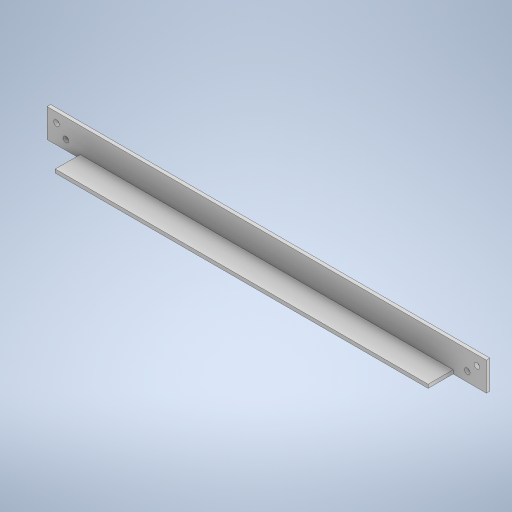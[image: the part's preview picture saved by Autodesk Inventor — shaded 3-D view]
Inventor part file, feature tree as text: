
AUTODESK INVENTOR PART (.ipt)
format: ipt  version: 2023 (Build 270158000, 158)  size: 284,672 bytes
history: native  units: in
note: dims shown in document units (in); Inventor stores cm internally (conversion verified against a paired STEP export)
features: extrude x3, sketch x3, mirror x1
ambient origin geometry x8: Origin, YZ Plane, XZ Plane, XY Plane, X Axis, Y Axis, Z Axis, Center Point
bodies: Solid1 (feature_tree)
feature tree (7):
  extrude  "Extrusion1"  Depth=0.125in
  extrude  "Extrusion2"  TaperAngle=0.0deg  [1 undecoded]
  extrude  "Extrusion3"  Depth=0.125in
  mirror  "Mirror1"
  sketch  "Sketch1"  dims[d1=1.0in d2=0.125in]
  sketch  "Sketch2"  dims[d3=15.3858in d4=0.0in]
  sketch  "Sketch3"  dims[d5=1.1644in d6=0.125in d7=0.0in d8=1.0in d9=0.125in d10=0.191in d11=0.3333in d12=0.125in d13=0.0in]
note: 1 required parameter value undecoded (feature->parameter linkage not recoverable at this tier; creation-order binding heuristic only, values carry confidence <= 0.55)
